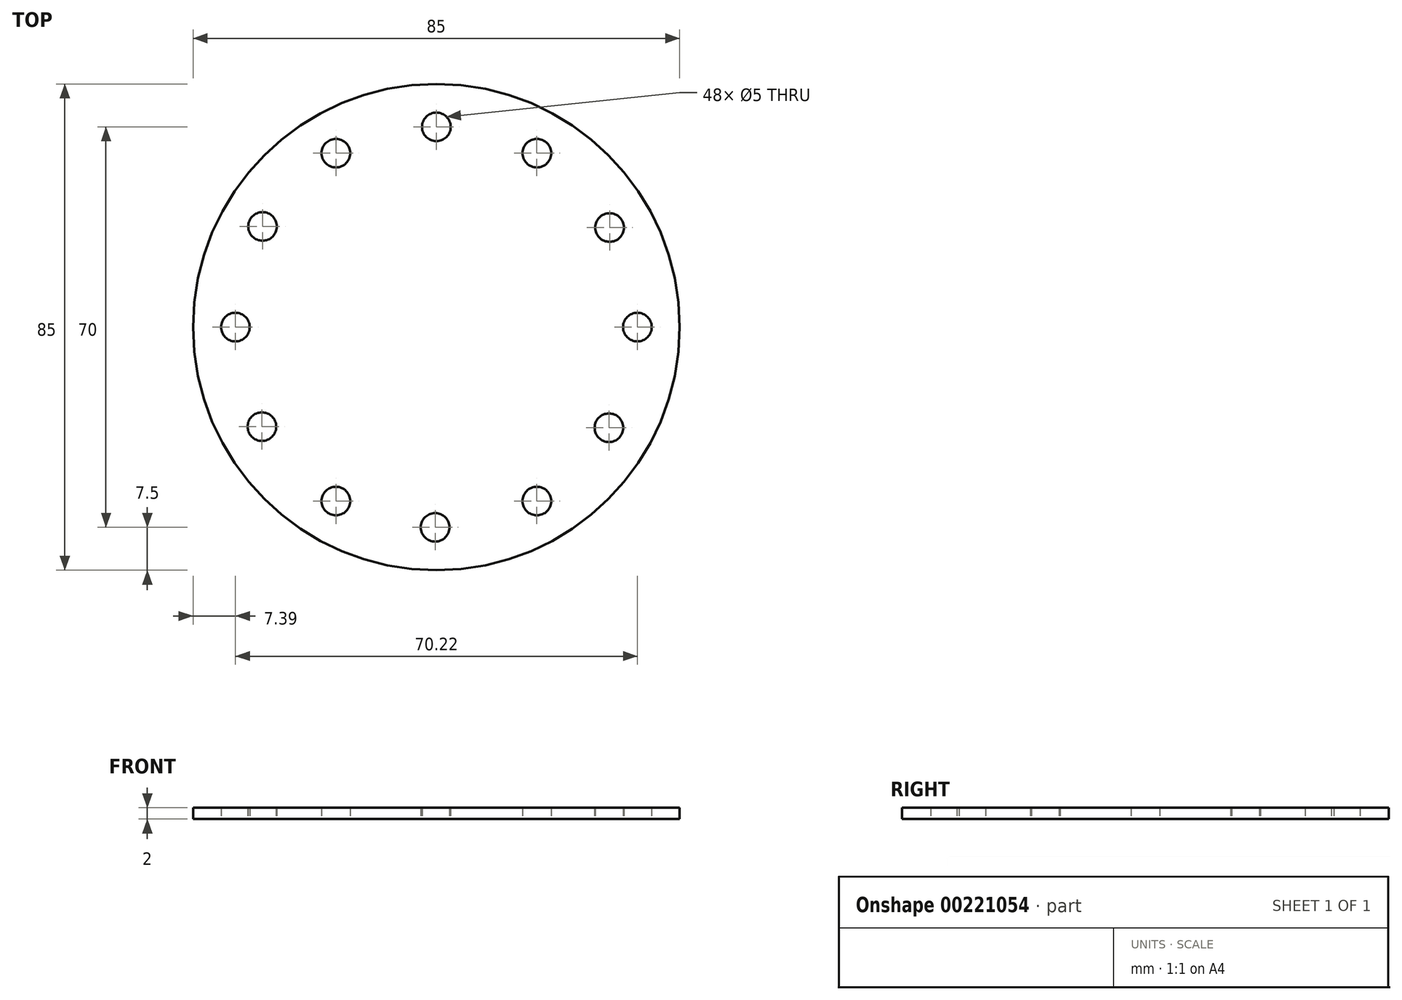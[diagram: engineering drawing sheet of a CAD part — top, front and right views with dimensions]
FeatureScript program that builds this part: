
annotation { "Feature Type Name" : "Feature", "Feature Type Description" : "" }
export const myFeature = defineFeature(function(context is Context, id is Id, definition is map)
    precondition{}
    {
        {
            var Q0;
            Q0=qCreatedBy(makeId("Top.planeOp"),FACE);
            var sketch = newSketch(context, id + "F0", { "sketchPlane" : qUnion([Q0])});
            skCircle(sketch, "E0", {"center": v(0, 0) * mm, "radius": 42.5 * mm});
            skCircle(sketch, "E1", {"center": v(0, 35) * mm, "radius": 2.5 * mm});
            skCircle(sketch, "E2.1.0", {"center": v(-30.37, 17.6) * mm, "radius": 2.5 * mm});
            skCircle(sketch, "E2.2.0", {"center": v(-30.48, -17.4) * mm, "radius": 2.5 * mm});
            skCircle(sketch, "E2.3.0", {"center": v(-0.22, -35) * mm, "radius": 2.5 * mm});
            skCircle(sketch, "E2.4.0", {"center": v(30.15, -17.6) * mm, "radius": 2.5 * mm});
            skCircle(sketch, "E2.5.0", {"center": v(30.26, 17.4) * mm, "radius": 2.5 * mm});
            skPoint(sketch, "E2.center", {"position": v(-0.11, 0) * mm});
            skCircle(sketch, "E3", {"center": v(-35.11, 0) * mm, "radius": 2.5 * mm});
            skCircle(sketch, "E4.1.0", {"center": v(-17.56, -30.4) * mm, "radius": 2.5 * mm});
            skCircle(sketch, "E4.2.0", {"center": v(17.56, -30.4) * mm, "radius": 2.5 * mm});
            skCircle(sketch, "E4.3.0", {"center": v(35.11, 0) * mm, "radius": 2.5 * mm});
            skCircle(sketch, "E4.4.0", {"center": v(17.56, 30.4) * mm, "radius": 2.5 * mm});
            skCircle(sketch, "E4.5.0", {"center": v(-17.56, 30.4) * mm, "radius": 2.5 * mm});
            skSolve(sketch);
        }
        {
            var Q0;
            Q0=makeQuery(id+"F0.imprint","IMPRINT",FACE,{"disambiguationData":[TD([[makeQuery(id+"F0.imprint","IMPRINT",EDGE,{"derivedFrom":sQuery(id+"F0.wireOp",EDGE,"E0")}),1.0]])]});
            extrude(context, id + "F1", {"entities" : qUnion([Q0]), "depth" : 2 * mm});
        }
    });
